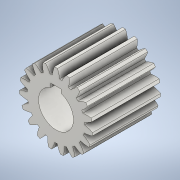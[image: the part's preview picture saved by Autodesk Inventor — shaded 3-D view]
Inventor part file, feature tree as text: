
AUTODESK INVENTOR PART (.ipt)
format: ipt  version: 2020 (Build 240168000, 168)  size: 247,808 bytes
history: native  units: mm (DEFAULTED — no unit token found)
features: plane x3, sketch x3, extrude x2, other x2
ambient origin geometry x8: Origin, YZ Plane, XZ Plane, XY Plane, X Axis, Y Axis, Z Axis, Center Point
bodies: Solid1 (feature_tree)
feature tree (10):
  extrude  "Extrusion1"  Depth=78.0mm TaperAngle=0.0deg
  plane  "Work Plane2"
  plane  "Work Plane8"
  plane  "Work Plane9"
  other  "正齿轮"
  extrude  "拉伸2"  Depth=10.0mm TaperAngle=0.0deg
  sketch  "Sketch1"  dims[d0=84.0mm d1=78.0mm d2=0.0mm]
  sketch  "Sketch2"  dims[d3=76.0mm d4=10.0mm d5=0.0mm]
  other  "Srf1"
  sketch  "草图3"  dims[d16=276.0mm d17=0.0mm d34=1.65347mm d39=0.0mm d41=0.0mm d43=276.0mm d46=276.0mm d47=0.0mm d48=0.0mm d49=40.0mm d50=12.0mm d51=8.0mm d52=3.5mm d53=10.0mm d54=0.0mm]
